# Revit family: Deckel_ungelocht_für_Kabelrinne_und_Kabelleiter_Russia
name_source: partatom
category: Generic Models
revit_build: Autodesk Revit 2015 (Build: 20140606_1530(x64)
units: mm (PartAtom-declared; Revit-internal decimal feet)

## types (7) — shared parameters
Manufacturer = OBO Bettermann
Material = Steel, Galvanized
URL = http://www.obo-bettermann.com

## per-type parameters (varying)
| type | "B" Dimension | GTIN | Manufacturer Art. No. |
| DRLU 100 FS RU | 102 mm | 4012196606290 | 6052021 |
| DRLU 150 FS RU | 152 mm  [stored 0.498688 ft] | 4012196649440 | 6052022 |
| DRLU 200 FS RU | 202 mm  [stored 0.66273 ft] | 4012196606306 | 6052023 |
| DRLU 300 FS RU | 302 mm  [stored 0.990814 ft] | 4012196606313 | 6052025 |
| DRLU 400 FS RU | 402 mm  [stored 1.3189 ft] | 4012196626298 | 6052027 |
| DRLU 500 FS RU | 502 mm  [stored 1.64698 ft] | 4012196626304 | 6052031 |
| DRLU 600 FS RU | 602 mm  [stored 1.97507 ft] | 4012196626311 | 6052033 |

note: column(s) folded — value = type name in every type: Article Type

note: [stored X ft] marks values corroborated as IEEE doubles in the binary element streams (Revit-internal decimal feet)

## geometry (parser evidence)
native form markers: Sweep x2
no freeform markers — native parametric forms only
